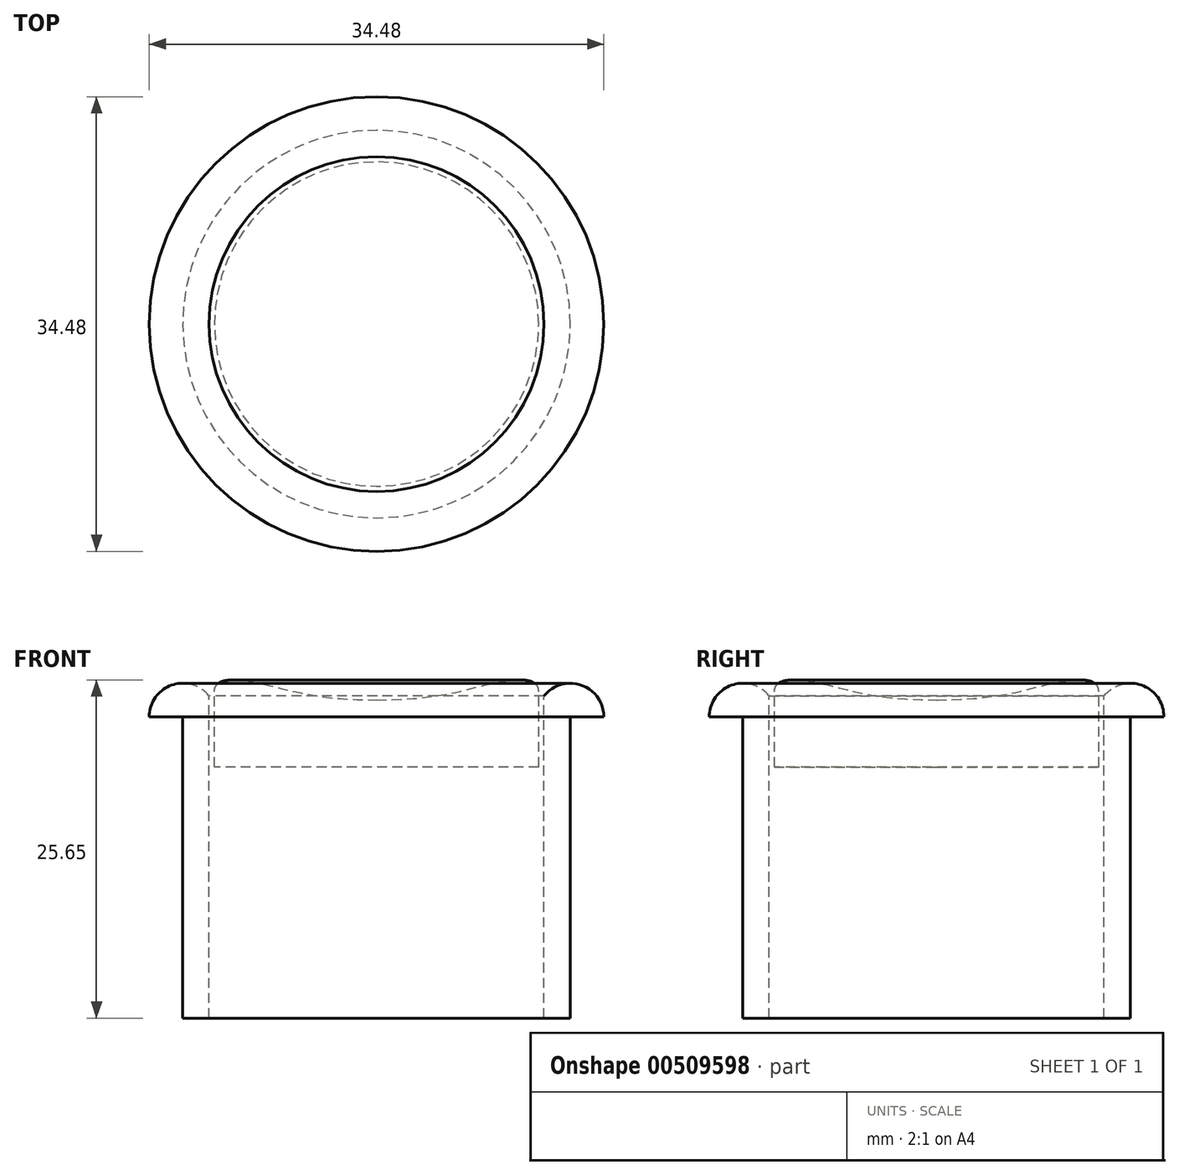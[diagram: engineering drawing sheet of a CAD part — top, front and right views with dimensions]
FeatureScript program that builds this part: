
annotation { "Feature Type Name" : "Feature", "Feature Type Description" : "" }
export const myFeature = defineFeature(function(context is Context, id is Id, definition is map)
    precondition{}
    {
        {
            var Q0;
            Q0=qCreatedBy(makeId("Front.planeOp"),FACE);
            var sketch = newSketch(context, id + "F0", { "sketchPlane" : qUnion([Q0])});
            skLineSegment(sketch, "E0", {"start": v(-14.7, -25.4) * mm, "end": v(-12.7, -25.4) * mm});
            skLineSegment(sketch, "E1", {"start": v(-12.7, -25.4) * mm, "end": v(-12.7, -0.97) * mm});
            skLineSegment(sketch, "E2", {"start": v(-14.7, -25.4) * mm, "end": v(-14.7, -2.54) * mm});
            skLineSegment(sketch, "E3", {"start": v(-14.7, -2.54) * mm, "end": v(-17.24, -2.54) * mm});
            skArc(sketch, "E4", {"start": v(-12.7, -0.97) * mm, "mid": v(-15.53, -0.14) * mm, "end": v(-17.24, -2.54) * mm});
            skLineSegment(sketch, "E5", {"start": v(19.49, 0) * mm, "end": v(-19.49, 0) * mm, "construction": true});
            skLineSegment(sketch, "E6", {"start": v(0, 22.94) * mm, "end": v(0, -22.94) * mm, "construction": true});
            skLineSegment(sketch, "E7", {"start": v(-12.3, -0.64) * mm, "end": v(-12.3, -6.35) * mm});
            skLineSegment(sketch, "E8", {"start": v(-12.3, -6.35) * mm, "end": v(0, -6.35) * mm});
            skFitSpline(sketch, "E9", {"points": [v(-12.3, -0.64) * mm, v(-8.88, 0) * mm, v(0, -1.27) * mm], "startDerivative": vector(0, 9.22) * mm, "endDerivative": vector(23.48, 0) * mm});
            skLineSegment(sketch, "E10", {"start": v(0, -1.27) * mm, "end": v(0, -6.35) * mm});
            skSolve(sketch);
        }
        {
            var Q0;
            Q0=makeQuery(id+"F0.imprint","IMPRINT",FACE,{"disambiguationData":[TD([[makeQuery(id+"F0.imprint","IMPRINT",EDGE,{"derivedFrom":sQuery(id+"F0.wireOp",EDGE,"E0")}),1.0]])]});
            var Q1;
            Q1=sQuery(id+"F0.wireOp",EDGE,"E6");
            revolve(context, id + "F1", {"entities" : qUnion([Q0]), "axis" : qUnion([Q1]), "revolveType" : RevolveType.FULL});
        }
        {
            var Q0;
            Q0=makeQuery(id+"F0.imprint","IMPRINT",FACE,{"disambiguationData":[TD([[makeQuery(id+"F0.imprint","IMPRINT",EDGE,{"derivedFrom":sQuery(id+"F0.wireOp",EDGE,"E7")}),1.0]])]});
            var Q1;
            Q1=sQuery(id+"F0.wireOp",EDGE,"E6");
            revolve(context, id + "F2", {"entities" : qUnion([Q0]), "axis" : qUnion([Q1]), "revolveType" : RevolveType.FULL});
        }
    });
